# Revit family: IS_iLifeA_T4719_BIM_NL
name_source: partatom
category: Plumbing Fixtures
units: mm (PartAtom-declared; Revit-internal decimal feet)

## family parameters
Always vertical = No
Cut with Voids When Loaded = No
OmniClass Number = 23.45.05.21.11.11
OmniClass Title = Water Operated Water Closets
Part Type = Normal
Room Calculation Point = No
Round Connector Dimension = Use Diameter
Shared = No
Work Plane-Based = No

## types (1)
- T471901 - I.life A back-to-wall bowl RimLS+ - White
    Accesoires = https://www.idealstandard.nl
    Accessories = https://www.idealstandard.nl
    Afmetingen = 540 x 400 x 355mm
    AfstandsEenheid = millimeter
    Afwerking = Weiß
    AreaMeasurement = internal
    AreaUnits = Millimeter
    Artikelnummer = T471901
    Artikelomschrijving = I.life A Vorwandschale RimLS+ - Weiß
    Artikelreferentie = I.life A Vorwandschale RimLS+
    Auteur = Ideal Standard
    BIMObjectName = IS_IdealStandard_WCpans_I.life_T4719
    BIMobject category = Toilets
    BIMobject category code = sanitary-toilets
    BIMobject main category = Sanitary
    BIMobject main category code = sanitary
    BarCode = 8014140486961
    Barcode = 8014140486961
    Beschrijvinggarantie = Herstellergarantie
    BimObjectNaam = IS_IdealStandard_WCpans_I.life_T4719
    Brand = Ideal Standard
    Brand url = http://https:
    Breedte = 0
    BrutoGewicht = 0
    Color = Weiß
    ConnectionType = Plumbing
    Cost = 0 $
    CurrencyUnit = €
    CurrentRevision = 1
    Date of publishing = 28/06/2021
    Description = I.life A Vorwandschale RimLS+ - Weiß
    Diepte = 0 mm  [stored 0 ft]
    DrainSize = 0 mm  [stored 0 ft]
    DurationUnit = Years
    DuurEenheid = Jaar
    Edition number = 1
    Eigenschappen = Vorwand-WC-SchüsselrandLS+
    Features = Back-to-wall WC Bowl RimLS+
    Finish = Weiß
    GTIN code = https://8014140486961
    Garantieonderdelen = 5
    Garantieunits = Jaar
    GemaaktOp = 40722
    GrootteAfvoergat = 0
    Help = https://www.idealstandard.nl
    Hoogte = 400.00082
    Hulp = https://www.idealstandard.nl
    IFC Classification = Sanitary Terminal
    IfcExportAs = IfcSanitaryTerminalType
    IfcExportType = TOILETPAN
    Installatieinstructies = https://www.idealstandard.nl
    Installation instructions = https://www.idealstandard.nl
    InstallationInstructions = https://www.idealstandard.nl
    Kleur = Weiß
    Kleurwc = Weiß
    Lengte = 540 mm
    LinearUnits = millimeter
    MainColor = White
    MaintenanceInformation = https://www.idealstandard.nl
    Manufacturer = Ideal Standard
    Manufacturer name = Ideal Standard
    ManufacturerURL = https://www.idealstandard.nl
    Masterformat 2014 Code = 12 46 16
    Masterformat 2014 Description = Bowls
    Materiaal = Vitrous China
    MateriaalWC = Vitrous China
    Material = Vitrous China
    Material main = Vitrous China
    Merk = Ideal Standard
    Model = T471901
    ModelNumber = T471901
    ModelReference = I.life A back-to-wall bowl RimLS+
    Montageinstuctie = https://www.idealstandard.nl
    NBS Reference Code = 45-35-70/384
    NBS Reference Description = WC pans
    Name = WCpans_I.life_T4719_IdealStandard
    NettWeight = 22
    Nettogewicht = 22
    NominalDepth = 540 mm
    NominalHeight = 400 mm  [stored 1.31234 ft]
    NominalWidth = 354 mm
    Normen = WCpans_I.life_T4719_IdealStandard
    OmniClass Code = 23-31 19 00
    OmniClass Description = Toilets
    OppervlakteEenheid = Millimeter
    Overloop = 0 mm  [stored 0 ft]
    PanColor = White
    PanMaterial = Vitrous China
    PanMounting = Back-to-wall
    Product Guid = ccfd8e93-b61f-4d57-8ede-217b013300d5
    Product SKU = T4719
    Product certification = https://www.idealstandard.nl
    Product data url = https://bimobject.com
    Product family = I.life
    Product group = Bowl
    Product name = I.life A back-to-wall bowl RimLS+
    Product url = https://www.idealstandard.nl
    ProductInformation = https://www.idealstandard.nl
    ProductSoort = WC-Schüssel
    Productinformatie = https://www.idealstandard.nl
    QR code = http://bimobject.com
    Referentie = I.life A Vorwandschale RimLS+
    Revisie = 1
    Shape = sculpture
    Size = 540 x 400 x 355mm
    Space = Internal
    SpareParts = https://www.idealstandard.nl
    Technical description = https://www.idealstandard.nl
    Telefoonnummer = 077 355 08 08
    ToiletPanType = back-to-wall bowl
    ToiletType = back-to-wall bowl
    TypeWC = back-to-wall bowl
    Typeconnectie = Installation
    TypespoelingWC = abwaschen spülen
    UNSPSC Code = 30181511
    URL = https://https:
    Uniclass 1.4 Code = L7216
    Uniclass 1.4 Description = Toilets
    Uniclass 2.0 Code = PR-35-93-94
    Uniclass 2.0 Description = Wc Pans
    Uniclass 2015 Code = Pr_40_20_93_94
    Uniclass 2015 Name = WC pans
    Uniclass2015Beschrijving = WC pans
    Uniclass2015Code = Pr_40_20_93_94
    Uniclass2015Referentie = Pr_40_20_93_94
    Uniclass2015Title = WC pans
    Uniclass2015Version = v1.20
    Urlproducent = https://https:
    ValutaEenheid = €
    Versie = 1
    Version = 1
    Vervangingskosten = 0
    VolumeUnits = Liter
    Volumeunits = Liter
    Vorm = beeldhouwwerk
    WRASURL = https://www.wrasapprovals.co.uk
    WarrantyDescription = manufacturer warranty
    WarrantyDurationParts = 99
    WarrantyDurationUnit = years
    Wisselstukken = https://www.idealstandard.nl
    Youtube clip = https://www.youtube.com

note: [stored X ft] marks values corroborated as IEEE doubles in the binary element streams (Revit-internal decimal feet)

## geometry (parser evidence)
native form markers: Sweep x3
no freeform markers — native parametric forms only
